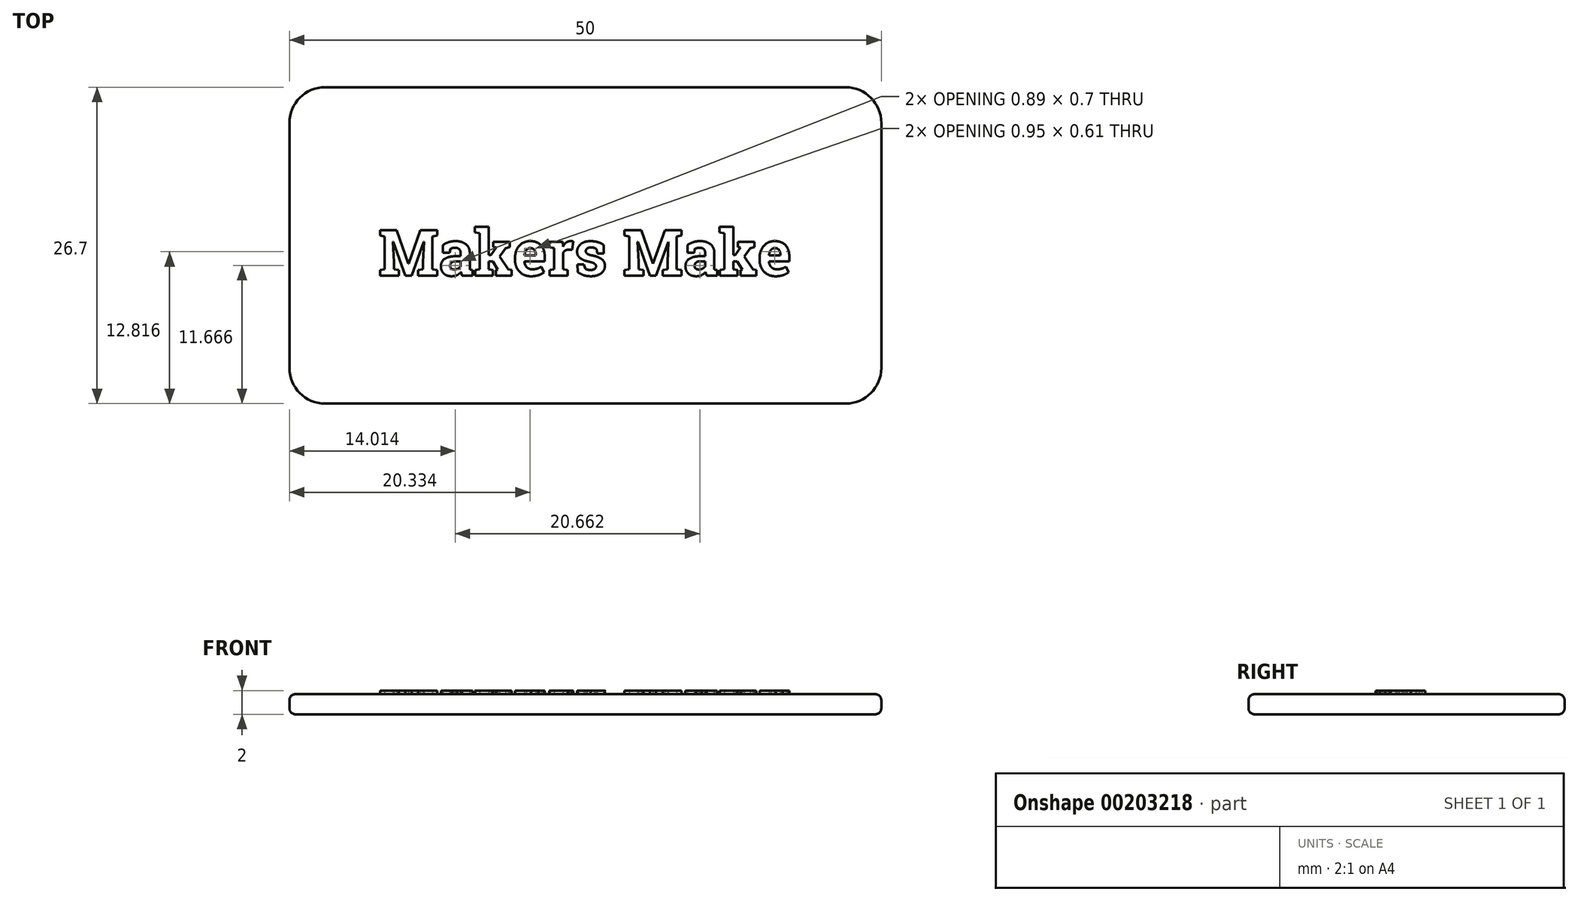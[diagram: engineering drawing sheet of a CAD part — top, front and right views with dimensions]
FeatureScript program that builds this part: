
annotation { "Feature Type Name" : "Feature", "Feature Type Description" : "" }
export const myFeature = defineFeature(function(context is Context, id is Id, definition is map)
    precondition{}
    {
        {
            var Q0;
            Q0=qCreatedBy(makeId("Top.planeOp"),FACE);
            var sketch = newSketch(context, id + "F0", { "sketchPlane" : qUnion([Q0])});
            skLineSegment(sketch, "E0", {"start": v(0, 3) * mm, "end": v(0, 23.7) * mm});
            skLineSegment(sketch, "E1", {"start": v(-3, 26.7) * mm, "end": v(-47, 26.7) * mm});
            skLineSegment(sketch, "E2", {"start": v(-50, 23.7) * mm, "end": v(-50, 3) * mm});
            skLineSegment(sketch, "E3", {"start": v(-47, 0) * mm, "end": v(-3, 0) * mm});
            skPoint(sketch, "E4.visualSharp", {"position": v(-50, 0) * mm});
            skArc(sketch, "E4.filletArc", {"start": v(-50, 3) * mm, "mid": v(-49.12, 0.88) * mm, "end": v(-47, 0) * mm});
            skPoint(sketch, "E5.visualSharp", {"position": v(-50, 26.7) * mm});
            skArc(sketch, "E5.filletArc", {"start": v(-47, 26.7) * mm, "mid": v(-49.12, 25.82) * mm, "end": v(-50, 23.7) * mm});
            skPoint(sketch, "E6.visualSharp", {"position": v(0, 26.7) * mm});
            skArc(sketch, "E6.filletArc", {"start": v(0, 23.7) * mm, "mid": v(-0.88, 25.82) * mm, "end": v(-3, 26.7) * mm});
            skPoint(sketch, "E7.visualSharp", {"position": v(0, 0) * mm});
            skArc(sketch, "E7.filletArc", {"start": v(-3, 0) * mm, "mid": v(-0.88, 0.88) * mm, "end": v(0, 3) * mm});
            skSolve(sketch);
        }
        {
            var Q0;
            Q0=makeQuery(id+"F0.imprint","IMPRINT",FACE,{"disambiguationData":[TD([[makeQuery(id+"F0.imprint","IMPRINT",EDGE,{"derivedFrom":sQuery(id+"F0.wireOp",EDGE,"E0")}),1.0]])]});
            extrude(context, id + "F1", {"entities" : qUnion([Q0]), "depth" : 1.7 * mm});
        }
        {
            var Q0;
            Q0=makeQuery(id+"F1.opExtrude","CAP_EDGE",EDGE,{"disambiguationData":[OSD([sQuery(id+"F0.wireOp",EDGE,"E3")])],"isStart":false});
            var Q1;
            Q1=makeQuery(id+"F1.opExtrude","CAP_EDGE",EDGE,{"disambiguationData":[OSD([sQuery(id+"F0.wireOp",EDGE,"E1")])],"isStart":true});
            fillet(context, id + "F2", {"entities" : qUnion([Q0, Q1]), "radius" : .5 * mm, "tangentPropagation" : true, "allowEdgeOverflow" : false});
        }
        {
            var Q0;
            Q0=makeQuery(id+"F1.opExtrude","CAP_FACE",FACE,{"disambiguationData":[OSD([sQuery(id+"F0.wireOp",EDGE,"E0"),sQuery(id+"F0.wireOp",EDGE,"E1"),sQuery(id+"F0.wireOp",EDGE,"E2"),sQuery(id+"F0.wireOp",EDGE,"E3"),sQuery(id+"F0.wireOp",EDGE,"E4.filletArc"),sQuery(id+"F0.wireOp",EDGE,"E5.filletArc"),sQuery(id+"F0.wireOp",EDGE,"E6.filletArc"),sQuery(id+"F0.wireOp",EDGE,"E7.filletArc")])],"isStart":false});
            var sketch = newSketch(context, id + "F3", { "sketchPlane" : qUnion([Q0])});
            skText(sketch, "E8", { "text": "Makers Make", "fontName": "RobotoSlab-Bold.ttf"});
            const initialGuessF3  = {"E8": [-0.0425, 0.0108, 1, 0, 0.0039]};
            skSetInitialGuess(sketch, initialGuessF3);
            skSolve(sketch);
        }
        {
            var Q0;
            Q0 = qSketchRegion(id + "F3", true);
            extrude(context, id + "F4", {"entities" : qUnion([Q0]), "depth" : .3 * mm});
        }
    });
